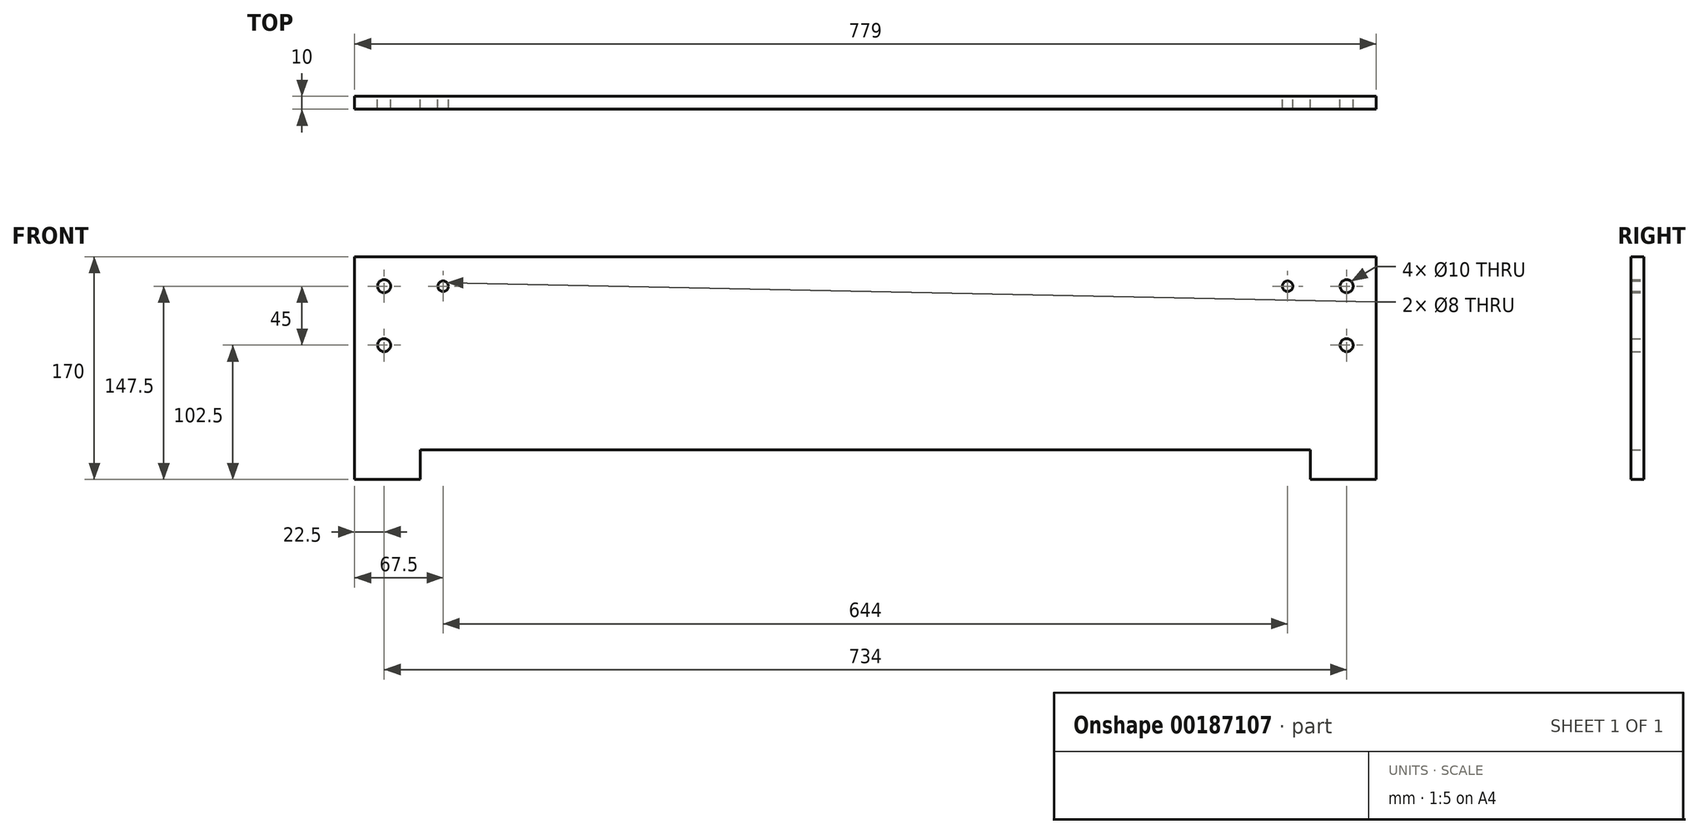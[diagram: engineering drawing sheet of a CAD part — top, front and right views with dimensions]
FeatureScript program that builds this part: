
annotation { "Feature Type Name" : "Feature", "Feature Type Description" : "" }
export const myFeature = defineFeature(function(context is Context, id is Id, definition is map)
    precondition{}
    {
        {
            var Q0;
            Q0=qCreatedBy(makeId("Front.planeOp"),FACE);
            var sketch = newSketch(context, id + "F0", { "sketchPlane" : qUnion([Q0])});
            skLineSegment(sketch, "E0.top", {"start": v(389.5, 80) * mm, "end": v(-389.5, 80) * mm});
            skLineSegment(sketch, "E0.left", {"start": v(389.5, -80) * mm, "end": v(389.5, 80) * mm});
            skLineSegment(sketch, "E0.right", {"start": v(-389.5, -80) * mm, "end": v(-389.5, 80) * mm});
            skPoint(sketch, "E0.middle", {"position": v(0, 0) * mm});
            skLineSegment(sketch, "E1", {"start": v(-339.5, -67.5) * mm, "end": v(-339.5, -80) * mm});
            skLineSegment(sketch, "E2", {"start": v(339.5, -67.5) * mm, "end": v(339.5, -80) * mm});
            skLineSegment(sketch, "E3", {"start": v(-339.5, -67.5) * mm, "end": v(339.5, -67.5) * mm});
            skCircle(sketch, "E4", {"center": v(-367, 57.5) * mm, "radius": 5 * mm});
            skCircle(sketch, "E5", {"center": v(-367, 12.5) * mm, "radius": 5 * mm});
            skCircle(sketch, "E6", {"center": v(-322, 57.5) * mm, "radius": 4 * mm});
            skCircle(sketch, "E7", {"center": v(367, 57.5) * mm, "radius": 5 * mm});
            skCircle(sketch, "E8", {"center": v(367, 12.5) * mm, "radius": 5 * mm});
            skCircle(sketch, "E9", {"center": v(322, 57.5) * mm, "radius": 4 * mm});
            skLineSegment(sketch, "E10", {"start": v(-389.5, -80) * mm, "end": v(-389.5, -90) * mm});
            skLineSegment(sketch, "E11", {"start": v(-389.5, -90) * mm, "end": v(-339.5, -90) * mm});
            skLineSegment(sketch, "E12", {"start": v(389.5, -90) * mm, "end": v(389.5, -80) * mm});
            skLineSegment(sketch, "E13", {"start": v(-339.5, -80) * mm, "end": v(-339.5, -90) * mm});
            skLineSegment(sketch, "E14", {"start": v(339.5, -80) * mm, "end": v(339.5, -90) * mm});
            skLineSegment(sketch, "E15.trimOffspring", {"start": v(339.5, -90) * mm, "end": v(389.5, -90) * mm});
            skSolve(sketch);
        }
        {
            var Q0;
            Q0=makeQuery(id+"F0.imprint","IMPRINT",FACE,{"disambiguationData":[TD([[makeQuery(id+"F0.imprint","IMPRINT",EDGE,{"derivedFrom":sQuery(id+"F0.wireOp",EDGE,"E0.top")}),1.0]])]});
            extrude(context, id + "F1", {"entities" : qUnion([Q0]), "depth" : 10 * mm});
        }
    });
